# Revit family: GR_Адаптер линейный_Муфта(1)_VL-F-КСД-У-О_R21
name_source: partatom
category: Соединительные детали воздуховодов
units: mm (PartAtom-declared; Revit-internal decimal feet)

## family parameters
Всегда вертикально = Да
Заголовок OmniClass = Metal Ducts
На основе рабочей плоскости = Нет
Номер OmniClass = 23.75.70.14.31
Общий = Нет
При загрузке вырезать с полостями = Нет
Размер круглого соединителя = Использовать диаметр
Тип детали = Мультипорт

## types (15) — shared parameters
ADSK_URL страницы изделия = https://grilles.ru
ADSK_Версия Revit = 2021
ADSK_Единица измерения = шт.
ADSK_Завод-изготовитель = ООО "ВЕНТРЕШЕТКИКОМ"
ADSK_Код изделия = 000191
ADSK_Количество = 1
ADSK_Материал = ADSK_Оцинкованная сталь
ADSK_Наименование = VL-F-КСД-У-О, адаптер вентиляционной решётки
Изготовитель = ООО "ВЕНТРЕШЕТКИКОМ"
Корпус_Металл_Толщина = 1 мм
Муфта_Металл_Толщина = 1 мм
zero-valued in all types: Отметка по умолчанию

## per-type parameters (varying)
| type | Корпус_Высота | Корпус_Длина | Решетка_отступ | Решётка_Высота |
| VL-F-КСД-У-О 1-20 | 130 мм | 174 мм | 28 мм | 54 мм |
| VL-F-КСД-У-О 1-30 | 130 мм | 184 мм | 33 мм | 64 мм |
| VL-F-КСД-У-О 1-40 | 130 мм | 194 мм | 38 мм | 74 мм |
| VL-F-КСД-У-О 1-50 | 130 мм | 204 мм | 43 мм | 84 мм |
| VL-F-КСД-У-О 1-60 | 170 мм | 214 мм | 48 мм | 94 мм |
| VL-F-КСД-У-О 1-70 | 170 мм | 224 мм | 53 мм | 104 мм |
| VL-F-КСД-У-О 2-20 | 130 мм | 214 мм | 48 мм | 94 мм |
| VL-F-КСД-У-О 2-25 | 130 мм | 224 мм | 53 мм | 104 мм |
| VL-F-КСД-У-О 2-30 | 130 мм | 234 мм | 58 мм | 114 мм |
| VL-F-КСД-У-О 3-20 | 130 мм | 254 мм | 68 мм | 134 мм |
| VL-F-КСД-У-О 3-25 | 130 мм | 269 мм | 76 мм | 149 мм |
| VL-F-КСД-У-О 3-30 | 130 мм | 284 мм | 83 мм | 164 мм |
| VL-F-КСД-У-О 4-20 | 170 мм | 294 мм | 88 мм | 174 мм |
| VL-F-КСД-У-О 4-25 | 170 мм | 314 мм | 98 мм | 194 мм |
| VL-F-КСД-У-О 4-30 | 170 мм | 334 мм | 108 мм | 214 мм |

note: column(s) folded — value = type name in every type: ADSK_Марка
